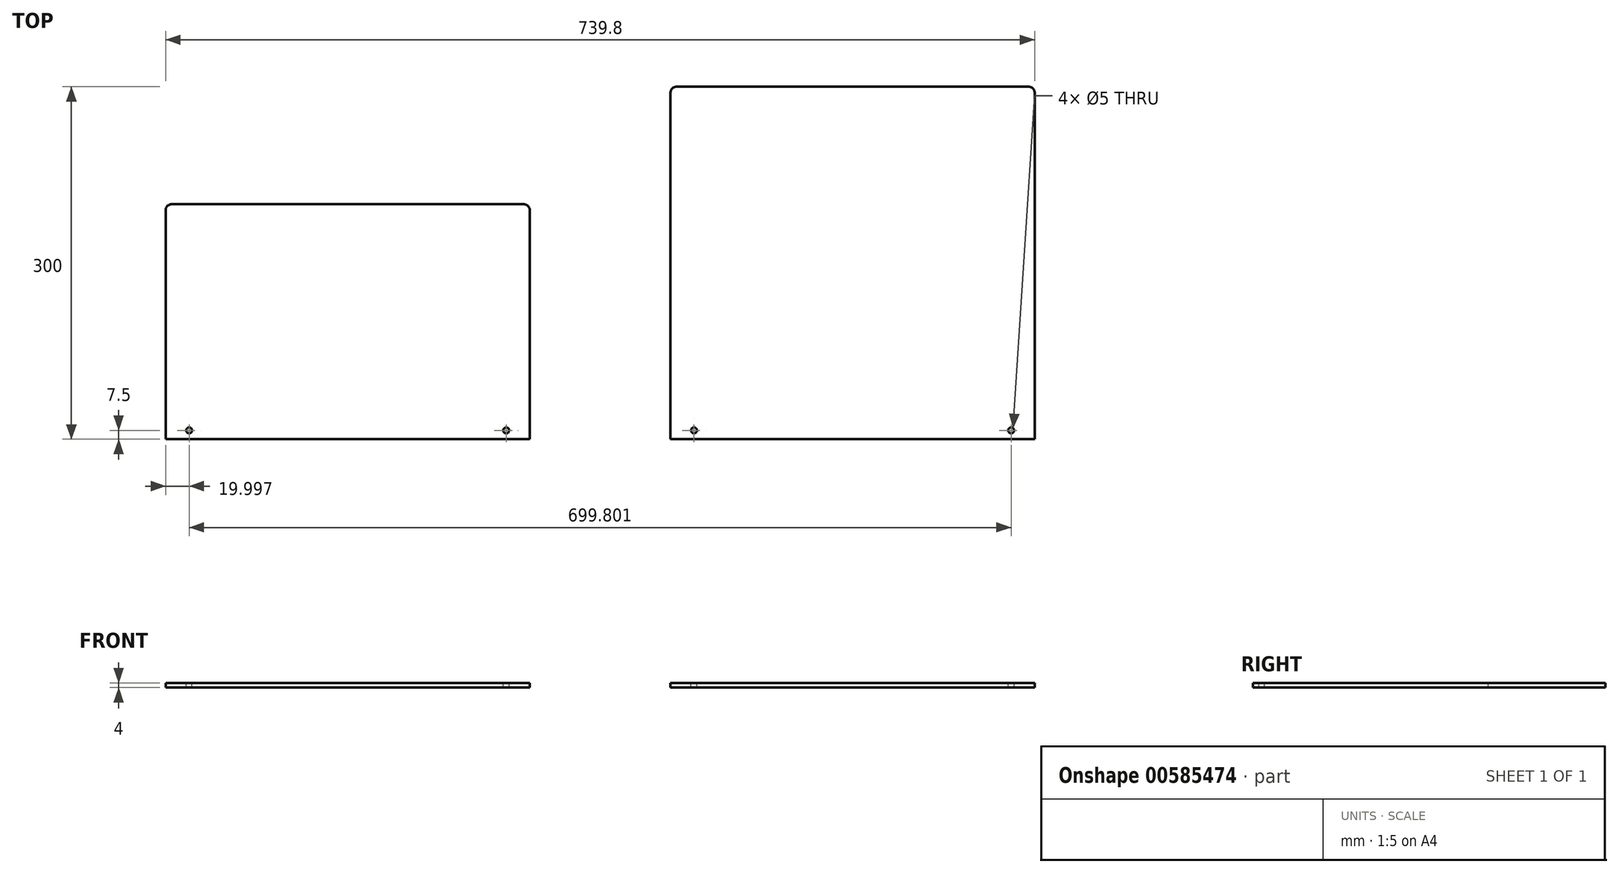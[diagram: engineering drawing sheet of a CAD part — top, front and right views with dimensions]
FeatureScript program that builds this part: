
annotation { "Feature Type Name" : "Feature", "Feature Type Description" : "" }
export const myFeature = defineFeature(function(context is Context, id is Id, definition is map)
    precondition{}
    {
        {
            var Q0;
            Q0=qCreatedBy(makeId("Top.planeOp"),FACE);
            var sketch = newSketch(context, id + "F0", { "sketchPlane" : qUnion([Q0])});
            skLineSegment(sketch, "E0.bottom", {"start": v(-363.18, 200) * mm, "end": v(-53.18, 200) * mm});
            skLineSegment(sketch, "E0.top", {"start": v(-363.18, 0) * mm, "end": v(-53.18, 0) * mm});
            skLineSegment(sketch, "E0.left", {"start": v(-363.18, 200) * mm, "end": v(-363.18, 0) * mm});
            skLineSegment(sketch, "E0.right", {"start": v(-53.18, 200) * mm, "end": v(-53.18, 0) * mm});
            skLineSegment(sketch, "E1.bottom", {"start": v(66.62, 300) * mm, "end": v(376.62, 300) * mm});
            skLineSegment(sketch, "E1.top", {"start": v(66.62, 0) * mm, "end": v(376.62, 0) * mm});
            skLineSegment(sketch, "E1.left", {"start": v(66.62, 300) * mm, "end": v(66.62, 0) * mm});
            skLineSegment(sketch, "E1.right", {"start": v(376.62, 300) * mm, "end": v(376.62, 0) * mm});
            skSolve(sketch);
        }
        {
            var Q0;
            Q0 = qSketchRegion(id + "F0", true);
            extrude(context, id + "F1", {"entities" : qUnion([Q0]), "depth" : 4 * mm, "offsetDistance" : 25 * mm});
        }
        {
            var Q0;
            Q0=makeQuery(id+"F1.opExtrude","CAP_FACE",FACE,{"disambiguationData":[OSD([sQuery(id+"F0.wireOp",EDGE,"E1.bottom"),sQuery(id+"F0.wireOp",EDGE,"E1.top"),sQuery(id+"F0.wireOp",EDGE,"E1.left"),sQuery(id+"F0.wireOp",EDGE,"E1.right")])],"isStart":false});
            var sketch = newSketch(context, id + "F2", { "sketchPlane" : qUnion([Q0])});
            skLineSegment(sketch, "E2", {"start": v(356.62, 0) * mm, "end": v(356.62, 7.5) * mm});
            skSolve(sketch);
        }
        {
            var Q0;
            Q0=sQuery(id+"F2.wireOp",VERTEX,"E2.end");
            var Q1;
            Q1=makeQuery(id+"F1.opExtrude","SWEPT_BODY",BODY,{"disambiguationData":[OSD([sQuery(id+"F0.wireOp",EDGE,"E1.bottom"),sQuery(id+"F0.wireOp",EDGE,"E1.top"),sQuery(id+"F0.wireOp",EDGE,"E1.left"),sQuery(id+"F0.wireOp",EDGE,"E1.right")])]});
            hole(context, id + "F3", {"style" : HoleStyle.SIMPLE, "endStyle" : HoleEndStyle.THROUGH, "holeDiameter" : 5 * mm, "majorDiameter" : 5 * mm, "isTappedThrough" : true, "tappedDepth" : 12 * mm, "tapClearance" : 3, "locations" : qUnion([Q0]), "scope" : qUnion([Q1])});
        }
        {
            var Q0;
            Q0=makeQuery(id+"F1.opExtrude","CAP_FACE",FACE,{"disambiguationData":[OSD([sQuery(id+"F0.wireOp",EDGE,"E1.bottom"),sQuery(id+"F0.wireOp",EDGE,"E1.top"),sQuery(id+"F0.wireOp",EDGE,"E1.left"),sQuery(id+"F0.wireOp",EDGE,"E1.right")])],"isStart":false});
            var sketch = newSketch(context, id + "F4", { "sketchPlane" : qUnion([Q0])});
            skLineSegment(sketch, "E3", {"start": v(86.62, 0) * mm, "end": v(86.62, 7.5) * mm});
            skSolve(sketch);
        }
        {
            var Q0;
            Q0=sQuery(id+"F4.wireOp",VERTEX,"E3.end");
            var Q1;
            Q1=makeQuery(id+"F1.opExtrude","SWEPT_BODY",BODY,{"disambiguationData":[OSD([sQuery(id+"F0.wireOp",EDGE,"E1.bottom"),sQuery(id+"F0.wireOp",EDGE,"E1.top"),sQuery(id+"F0.wireOp",EDGE,"E1.left"),sQuery(id+"F0.wireOp",EDGE,"E1.right")])]});
            hole(context, id + "F5", {"style" : HoleStyle.SIMPLE, "endStyle" : HoleEndStyle.THROUGH, "holeDiameter" : 5 * mm, "majorDiameter" : 5 * mm, "isTappedThrough" : true, "tappedDepth" : 12 * mm, "tapClearance" : 3, "locations" : qUnion([Q0]), "scope" : qUnion([Q1])});
        }
        {
            var Q0;
            Q0=makeQuery(id+"F1.opExtrude","CAP_FACE",FACE,{"disambiguationData":[OSD([sQuery(id+"F0.wireOp",EDGE,"E0.bottom"),sQuery(id+"F0.wireOp",EDGE,"E0.top"),sQuery(id+"F0.wireOp",EDGE,"E0.left"),sQuery(id+"F0.wireOp",EDGE,"E0.right")])],"isStart":false});
            var sketch = newSketch(context, id + "F6", { "sketchPlane" : qUnion([Q0])});
            skLineSegment(sketch, "E4", {"start": v(-73.18, 0) * mm, "end": v(-73.18, 7.5) * mm});
            skSolve(sketch);
        }
        {
            var Q0;
            Q0=sQuery(id+"F6.wireOp",VERTEX,"E4.end");
            var Q1;
            Q1=makeQuery(id+"F1.opExtrude","SWEPT_BODY",BODY,{"disambiguationData":[OSD([sQuery(id+"F0.wireOp",EDGE,"E0.bottom"),sQuery(id+"F0.wireOp",EDGE,"E0.top"),sQuery(id+"F0.wireOp",EDGE,"E0.left"),sQuery(id+"F0.wireOp",EDGE,"E0.right")])]});
            hole(context, id + "F7", {"style" : HoleStyle.SIMPLE, "endStyle" : HoleEndStyle.THROUGH, "holeDiameter" : 5 * mm, "majorDiameter" : 5 * mm, "isTappedThrough" : true, "tappedDepth" : 12 * mm, "tapClearance" : 3, "locations" : qUnion([Q0]), "scope" : qUnion([Q1])});
        }
        {
            var Q0;
            Q0=makeQuery(id+"F1.opExtrude","CAP_FACE",FACE,{"disambiguationData":[OSD([sQuery(id+"F0.wireOp",EDGE,"E0.bottom"),sQuery(id+"F0.wireOp",EDGE,"E0.top"),sQuery(id+"F0.wireOp",EDGE,"E0.left"),sQuery(id+"F0.wireOp",EDGE,"E0.right")])],"isStart":false});
            var sketch = newSketch(context, id + "F8", { "sketchPlane" : qUnion([Q0])});
            skLineSegment(sketch, "E5", {"start": v(-343.18, 0) * mm, "end": v(-343.18, 7.5) * mm});
            skSolve(sketch);
        }
        {
            var Q0;
            Q0=sQuery(id+"F8.wireOp",VERTEX,"E5.end");
            var Q1;
            Q1=makeQuery(id+"F1.opExtrude","SWEPT_BODY",BODY,{"disambiguationData":[OSD([sQuery(id+"F0.wireOp",EDGE,"E0.bottom"),sQuery(id+"F0.wireOp",EDGE,"E0.top"),sQuery(id+"F0.wireOp",EDGE,"E0.left"),sQuery(id+"F0.wireOp",EDGE,"E0.right")])]});
            hole(context, id + "F9", {"style" : HoleStyle.SIMPLE, "endStyle" : HoleEndStyle.THROUGH, "holeDiameter" : 5 * mm, "majorDiameter" : 5 * mm, "isTappedThrough" : true, "tappedDepth" : 12 * mm, "tapClearance" : 3, "locations" : qUnion([Q0]), "scope" : qUnion([Q1])});
        }
        {
            var Q0;
            Q0=makeQuery(id+"F1.opExtrude","SWEPT_EDGE",EDGE,{"disambiguationData":[OSD([sQuery(id+"F0.wireOp",EDGE,"E0.bottom"),sQuery(id+"F0.wireOp",EDGE,"E0.left")])]});
            var Q1;
            Q1=makeQuery(id+"F1.opExtrude","SWEPT_EDGE",EDGE,{"disambiguationData":[OSD([sQuery(id+"F0.wireOp",EDGE,"E0.bottom"),sQuery(id+"F0.wireOp",EDGE,"E0.right")])]});
            var Q2;
            Q2=makeQuery(id+"F1.opExtrude","SWEPT_EDGE",EDGE,{"disambiguationData":[OSD([sQuery(id+"F0.wireOp",EDGE,"E1.bottom"),sQuery(id+"F0.wireOp",EDGE,"E1.left")])]});
            var Q3;
            Q3=makeQuery(id+"F1.opExtrude","SWEPT_EDGE",EDGE,{"disambiguationData":[OSD([sQuery(id+"F0.wireOp",EDGE,"E1.bottom"),sQuery(id+"F0.wireOp",EDGE,"E1.right")])]});
            fillet(context, id + "F10", {"entities" : qUnion([Q0, Q1, Q2, Q3]), "radius" : 5 * mm, "tangentPropagation" : true, "allowEdgeOverflow" : false});
        }
    });
